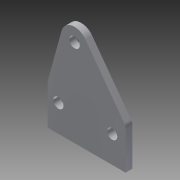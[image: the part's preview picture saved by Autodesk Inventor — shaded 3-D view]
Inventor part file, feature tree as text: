
AUTODESK INVENTOR PART (.ipt)
format: ipt  version: 2014 SP1 (Build 180222100, 222)  size: 101,888 bytes
history: native  units: in
note: dims shown in document units (in); Inventor stores cm internally (conversion verified against a paired STEP export)
features: extrude x1, fillet x1, sketch x1
ambient origin geometry x8: Origin, YZ Plane, XZ Plane, XY Plane, X Axis, Y Axis, Z Axis, Center Point
bodies: Solid1 (feature_tree)
feature tree (3):
  extrude  "Extrusion1"  Depth=0.125in TaperAngle=0.0deg
  fillet  "Fillet1"  Radius=0.5in
  sketch  "Sketch1"  dims[d1=0.19in d3=0.125in d4=0.0in d5=0.5in d6=0.25in d7=0.2in d9=0.25in d10=1.0in d14=0.5in d15=0.75in d16=0.194in d17=0.25in d18=0.125in]
